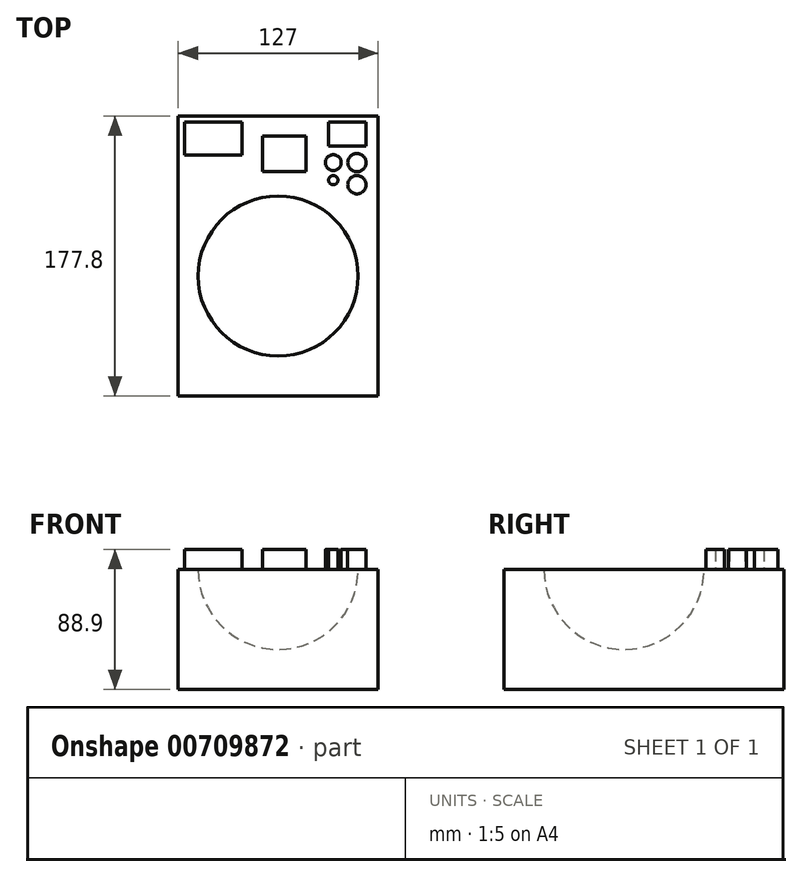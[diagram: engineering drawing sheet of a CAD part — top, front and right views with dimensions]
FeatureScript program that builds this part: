
annotation { "Feature Type Name" : "Feature", "Feature Type Description" : "" }
export const myFeature = defineFeature(function(context is Context, id is Id, definition is map)
    precondition{}
    {
        {
            var Q0;
            Q0=qCreatedBy(makeId("Top.planeOp"),FACE);
            var sketch = newSketch(context, id + "F0", { "sketchPlane" : qUnion([Q0])});
            skLineSegment(sketch, "E0.bottom", {"start": v(-63.5, 101.6) * mm, "end": v(63.5, 101.6) * mm});
            skLineSegment(sketch, "E0.top", {"start": v(-63.5, -76.2) * mm, "end": v(63.5, -76.2) * mm});
            skLineSegment(sketch, "E0.left", {"start": v(-63.5, 101.6) * mm, "end": v(-63.5, -76.2) * mm});
            skLineSegment(sketch, "E0.right", {"start": v(63.5, 101.6) * mm, "end": v(63.5, -76.2) * mm});
            skSolve(sketch);
        }
        {
            var Q0;
            Q0=makeQuery(id+"F0.imprint","IMPRINT",FACE,{"disambiguationData":[TD([[makeQuery(id+"F0.imprint","IMPRINT",EDGE,{"derivedFrom":sQuery(id+"F0.wireOp",EDGE,"E0.bottom")}),-1.0]])]});
            extrude(context, id + "F1", {"entities" : qUnion([Q0]), "oppositeDirection" : true, "depth" : 76.2 * mm, "offsetDistance" : 25.4 * mm});
        }
        {
            var Q0;
            Q0=makeQuery(id+"F1.opExtrude","CAP_FACE",FACE,{"disambiguationData":[OSD([sQuery(id+"F0.wireOp",EDGE,"E0.bottom"),sQuery(id+"F0.wireOp",EDGE,"E0.top"),sQuery(id+"F0.wireOp",EDGE,"E0.left"),sQuery(id+"F0.wireOp",EDGE,"E0.right")])],"isStart":true});
            var sketch = newSketch(context, id + "F2", { "sketchPlane" : qUnion([Q0])});
            skArc(sketch, "E1", {"start": v(0, -50.8) * mm, "mid": v(50.8, 0) * mm, "end": v(0, 50.8) * mm});
            skLineSegment(sketch, "E2", {"start": v(0, 101.6) * mm, "end": v(0, 50.8) * mm});
            skLineSegment(sketch, "E3", {"start": v(0, 50.8) * mm, "end": v(0, -50.8) * mm});
            skLineSegment(sketch, "E4", {"start": v(0, -50.8) * mm, "end": v(0, -76.2) * mm});
            skSolve(sketch);
        }
        {
            var Q0;
            Q0 = qSketchRegion(id + "F2", true);
            var Q1;
            Q1=sQuery(id+"F2.wireOp",EDGE,"E1");
            var Q2;
            Q2=sQuery(id+"F2.wireOp",EDGE,"E3");
            revolve(context, id + "F3", {"operationType" : NewBodyOperationType.REMOVE, "surfaceOperationType" : NewSurfaceOperationType.NEW, "entities" : qUnion([Q0]), "surfaceEntities" : qUnion([Q1]), "axis" : qUnion([Q2]), "revolveType" : RevolveType.FULL, "oppositeDirection" : true});
        }
        {
            var Q0;
            Q0=makeQuery(id+"F0.imprint","IMPRINT",FACE,{"disambiguationData":[TD([[makeQuery(id+"F0.imprint","IMPRINT",EDGE,{"derivedFrom":sQuery(id+"F0.wireOp",EDGE,"E0.bottom")}),-1.0]])]});
            var sketch = newSketch(context, id + "F4", { "sketchPlane" : qUnion([Q0])});
            skLineSegment(sketch, "E5.bottom", {"start": v(-59.38, 97.66) * mm, "end": v(-23.07, 97.66) * mm});
            skLineSegment(sketch, "E5.top", {"start": v(-59.38, 76.85) * mm, "end": v(-23.07, 76.85) * mm});
            skLineSegment(sketch, "E5.left", {"start": v(-59.38, 97.66) * mm, "end": v(-59.38, 76.85) * mm});
            skLineSegment(sketch, "E5.right", {"start": v(-23.07, 97.66) * mm, "end": v(-23.07, 76.85) * mm});
            skLineSegment(sketch, "E6.bottom", {"start": v(-10, 88.95) * mm, "end": v(17.58, 88.95) * mm});
            skLineSegment(sketch, "E6.top", {"start": v(-10, 66.2) * mm, "end": v(17.58, 66.2) * mm});
            skLineSegment(sketch, "E6.left", {"start": v(-10, 88.95) * mm, "end": v(-10, 66.2) * mm});
            skLineSegment(sketch, "E6.right", {"start": v(17.58, 88.95) * mm, "end": v(17.58, 66.2) * mm});
            skLineSegment(sketch, "E7.bottom", {"start": v(32.1, 97.66) * mm, "end": v(55.82, 97.66) * mm});
            skLineSegment(sketch, "E7.top", {"start": v(32.1, 82.65) * mm, "end": v(55.82, 82.65) * mm});
            skLineSegment(sketch, "E7.left", {"start": v(32.1, 97.66) * mm, "end": v(32.1, 82.65) * mm});
            skLineSegment(sketch, "E7.right", {"start": v(55.82, 97.66) * mm, "end": v(55.82, 82.65) * mm});
            skCircle(sketch, "E8", {"center": v(35, 72) * mm, "radius": 5.05 * mm});
            skCircle(sketch, "E9", {"center": v(50.01, 72) * mm, "radius": 5.8 * mm});
            skCircle(sketch, "E10", {"center": v(35, 60.87) * mm, "radius": 2.94 * mm});
            skCircle(sketch, "E11", {"center": v(50.01, 57.97) * mm, "radius": 5.8 * mm});
            skSolve(sketch);
        }
        {
            var Q0;
            Q0 = qSketchRegion(id + "F4", true);
            extrude(context, id + "F5", {"entities" : qUnion([Q0]), "operationType" : NewBodyOperationType.ADD, "depth" : 12.7 * mm, "offsetDistance" : 25.4 * mm});
        }
    });
